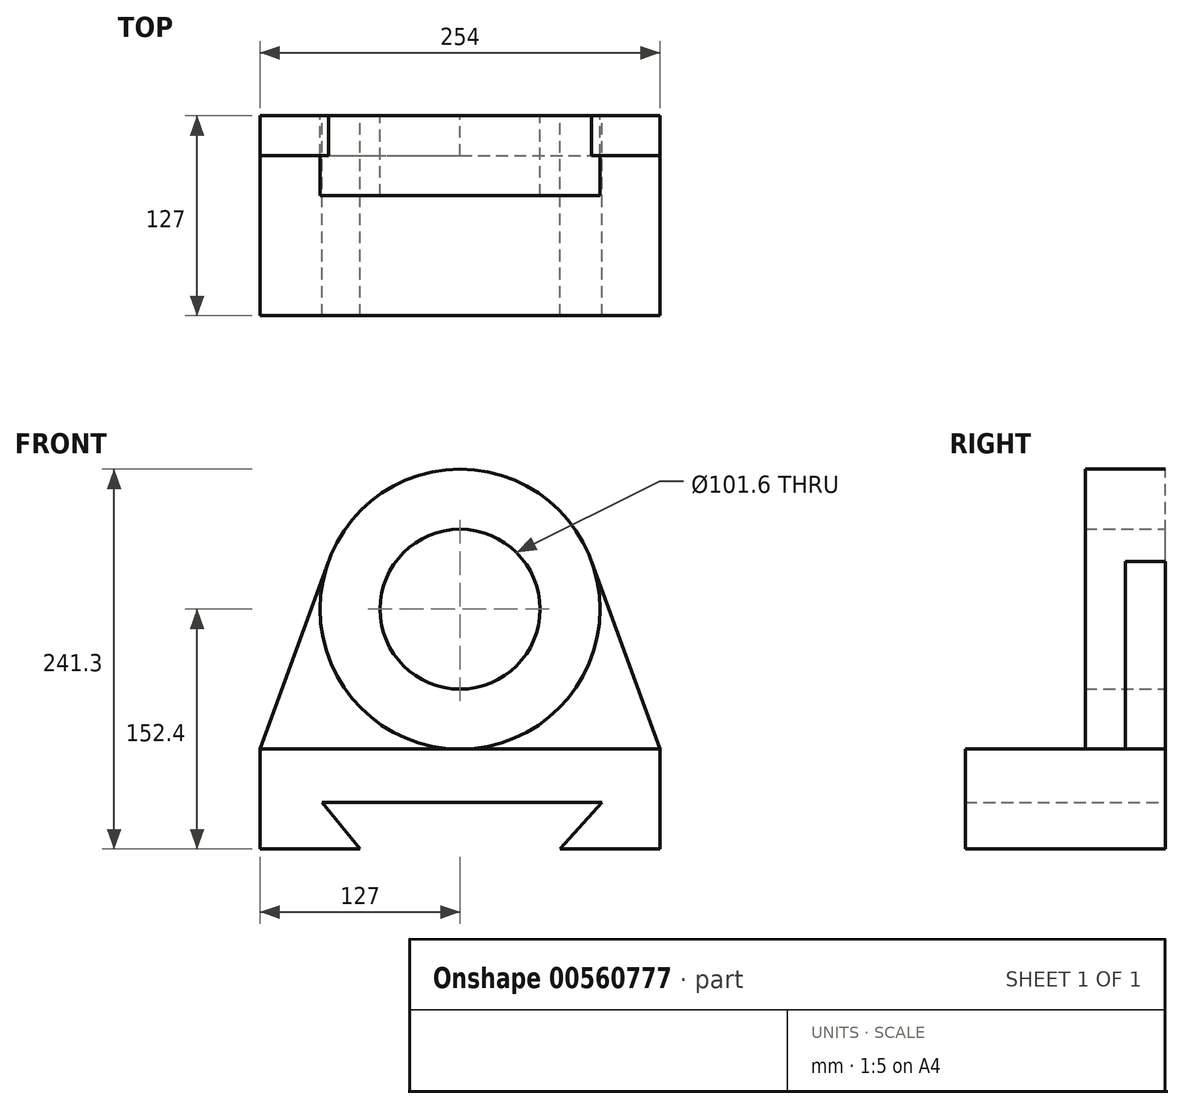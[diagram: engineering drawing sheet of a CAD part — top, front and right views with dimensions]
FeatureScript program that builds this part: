
annotation { "Feature Type Name" : "Feature", "Feature Type Description" : "" }
export const myFeature = defineFeature(function(context is Context, id is Id, definition is map)
    precondition{}
    {
        {
            var Q0;
            Q0=qCreatedBy(makeId("Front.planeOp"),FACE);
            var sketch = newSketch(context, id + "F0", { "sketchPlane" : qUnion([Q0])});
            skLineSegment(sketch, "E0", {"start": v(0, 0) * mm, "end": v(254, 0) * mm});
            skCircle(sketch, "E1", {"center": v(127, 88.9) * mm, "radius": 88.9 * mm});
            skPoint(sketch, "E1.centerSnap0", {"position": v(127, 0) * mm});
            skCircle(sketch, "E2", {"center": v(127, 88.9) * mm, "radius": 50.8 * mm});
            skLineSegment(sketch, "E3", {"start": v(0, 0) * mm, "end": v(43.47, 119.33) * mm});
            skLineSegment(sketch, "E4", {"start": v(254, 0) * mm, "end": v(210.53, 119.33) * mm});
            skLineSegment(sketch, "E5", {"start": v(0, 0) * mm, "end": v(0, -63.5) * mm});
            skLineSegment(sketch, "E6", {"start": v(254, 0) * mm, "end": v(254, -63.5) * mm});
            skLineSegment(sketch, "E7", {"start": v(254, -63.5) * mm, "end": v(190.5, -63.5) * mm});
            skLineSegment(sketch, "E8", {"start": v(0, -63.5) * mm, "end": v(63.5, -63.5) * mm});
            skLineSegment(sketch, "E9", {"start": v(63.5, -63.5) * mm, "end": v(39.44, -33.95) * mm});
            skLineSegment(sketch, "E10", {"start": v(39.44, -33.95) * mm, "end": v(217.24, -33.95) * mm});
            skLineSegment(sketch, "E11", {"start": v(217.24, -33.95) * mm, "end": v(190.5, -63.5) * mm});
            skSolve(sketch);
        }
        {
            var Q0;
            {var subQ0=sQuery(id+"F0.wireOp",EDGE,"E3");Q0=makeQuery(id+"F0.imprint","IMPRINT",FACE,{"disambiguationData":[TD([[makeQuery(id+"F0.imprint","IMPRINT",EDGE,{"derivedFrom":subQ0}),-1.0]])]});}
            var Q1;
            {var subQ0=sQuery(id+"F0.wireOp",EDGE,"E4");Q1=makeQuery(id+"F0.imprint","IMPRINT",FACE,{"disambiguationData":[TD([[makeQuery(id+"F0.imprint","IMPRINT",EDGE,{"derivedFrom":subQ0}),1.0]])]});}
            extrude(context, id + "F1", {"entities" : qUnion([Q0, Q1]), "depth" : 25.4 * mm, "offsetDistance" : 25.4 * mm});
        }
        {
            var Q0;
            {var subQ1=sQuery(id+"F0.wireOp",EDGE,"E5");Q0=makeQuery(id+"F0.imprint","IMPRINT",FACE,{"disambiguationData":[TD([[makeQuery(id+"F0.imprint","IMPRINT",EDGE,{"derivedFrom":subQ1}),1.0]])]});}
            extrude(context, id + "F2", {"entities" : qUnion([Q0]), "depth" : 127 * mm, "offsetDistance" : 25.4 * mm});
        }
        {
            var Q0;
            Q0=makeQuery(id+"F0.imprint","IMPRINT",FACE,{"disambiguationData":[TD([[makeQuery(id+"F0.imprint","IMPRINT",EDGE,{"derivedFrom":sQuery(id+"F0.wireOp",EDGE,"E2")}),-1.0]])]});
            extrude(context, id + "F3", {"entities" : qUnion([Q0]), "depth" : 50.8 * mm, "offsetDistance" : 25.4 * mm});
        }
    });
